# Revit family: Hager-Volta-IP30-Flush_mounted-syst-NoHosted-CH-de
name_source: partatom
category: Electrical Equipment
units: mm (PartAtom-declared; Revit-internal decimal feet)

## family parameters
Always vertical = Yes
Cut with Voids When Loaded = No
Panel Configuration = Two Columns, Circuits Across
Part Type = Panelboard
Room Calculation Point = No
Round Connector Dimension = Use Diameter
Shared = No
Work Plane-Based = Yes

## types (7) — shared parameters
Default Elevation = 1219 mm
EF000003 - Montageart = EV000383 - Unterputz
EF000007 - Farbe = EV000202 - weiß
EF000008 - Breite = 348 mm  [stored 1.14173 ft]
EF000049 - Tiefe = 98 mm  [stored 0.321522 ft]
EF000116 - RAL-Nummer = 9010
EF000118 - Mit Montageplatte = No
EF000218 - Einbautiefe = 89 mm  [stored 0.291995 ft]
EF000339 - Art der Abdeckung = EV004216 - Tür
EF000846 - Einbaubreite = 314 mm  [stored 1.03018 ft]
EF001062 - EMV-Ausführung = No
EF001088 - Anbaumöglichkeit = Yes
EF001131 - Innentiefe = 92 mm
EF001134 - DIN-Schiene = Yes
EF002950 - Breite in Teilungseinheiten = 12
EF004462 - Art der Schließung = EV000154 - sonstige
EF005474 - Schutzart (IP) = EV006410 - IP30
EF006244 - Transparenter Deckel/Tür = No
EF006306 - Mit Schloss = No
EF009212 - Ausführung Deckel = EV009916 - mit Ausschnitt
EF015777 - Neutralleiterklemmenblock = No
HG000001 - Anzahl der Spalten = 1
HG000002 - Mit tür = Yes
HG000003 - Bereich = Volta
HG000005 - Dicke = 3 mm  [stored 0.00984252 ft]
HG000006 - Unterputz = Yes
HG000009 - Doppelflügeligen Tür = No
HG000010 - Asymmetrische Türen = No
HG000011 - Leere Reihen von unten = No
HG000017 - Distanz zwischen den Polen = 18 mm  [stored 0.0590551 ft]
Manufacturer = Hager
Type Comments = Volta
zero-valued in all types: HG000007 - Anzahl der leeren Spalten, HG000008 - Anzahl der leeren Reihen

## per-type parameters (varying)
| type | EF000040 - Höhe | EF000266 - Anzahl der Reihen | EF000332 - Einbauhöhe | EF001596 - Werkstoff des Gehäuses | EF015776 - Erdungsklemmenblock | EF015941 - Signaldurchlassende Tür | HG000004 - Herstellerreferenz | Model |
| Unterputz IP30 B348 H356.5 T98 12 Teilungseinheiten - VU12NA | 356 mm | 1 | 321 mm | EV000139 - Kunststoff | Yes | No | VU12NA | VU12NA |
| Unterputz IP30 B348 H505.5 T98 12 Teilungseinheiten - VU24NA | 506 mm | 2 | 470 mm | EV000139 - Kunststoff | Yes | No | VU24NA | VU24NA |
| Unterputz IP30 B348 H630.5 T98 12 Teilungseinheiten - VU36NA | 630 mm | 3 | 595 mm | EV000139 - Kunststoff | Yes | No | VU36NA | VU36NA |
| Unterputz IP30 B348 H630.5 T98 12 Teilungseinheiten - VU36NRM | 630 mm | 3 | 595 mm | EV000139 - Kunststoff | No | Yes | VU36NRM | VU36NRM |
| Unterputz IP30 B348 H755.5 T98 12 Teilungseinheiten - VU48NA | 756 mm | 4 | 720 mm  [stored 2.3622 ft] | EV000139 - Kunststoff | Yes | No | VU48NA | VU48NA |
| Unterputz IP30 B348 H755.5 T98 12 Teilungseinheiten - VU48NRM | 756 mm | 4 | 720 mm  [stored 2.3622 ft] | EV000139 - Kunststoff | No | No | VU48NRM | VU48NRM |
| Unterputz IP30 B348 H880.5 T98 12 Teilungseinheiten - VU60NA | 880 mm  [stored 2.88714 ft] | 5 | 845 mm  [stored 2.77231 ft] | EV000154 - sonstige | Yes | No | VU60NA | VU60NA |

note: [stored X ft] marks values corroborated as IEEE doubles in the binary element streams (Revit-internal decimal feet)

## geometry (parser evidence)
native form markers: Sweep x13
no freeform markers — native parametric forms only
